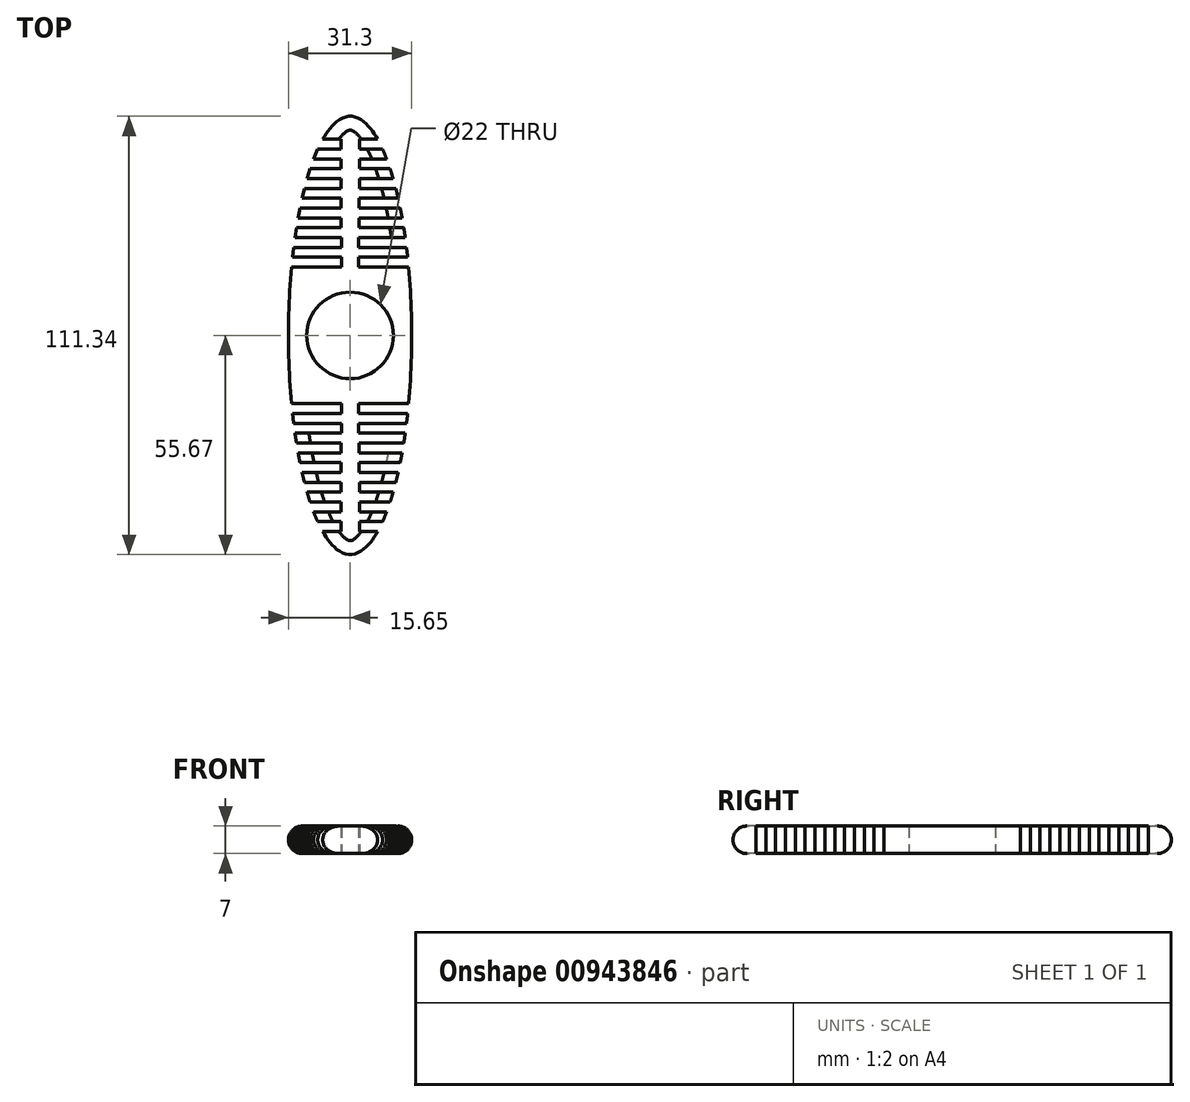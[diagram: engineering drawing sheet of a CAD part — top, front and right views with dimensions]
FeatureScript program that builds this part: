
annotation { "Feature Type Name" : "Feature", "Feature Type Description" : "" }
export const myFeature = defineFeature(function(context is Context, id is Id, definition is map)
    precondition{}
    {
        {
            var Q0;
            Q0=qCreatedBy(makeId("Top.planeOp"),FACE);
            var sketch = newSketch(context, id + "F0", { "sketchPlane" : qUnion([Q0])});
            skCircle(sketch, "E0", {"center": v(0, 0) * mm, "radius": 11 * mm});
            skEllipse(sketch, "E1", {"center": v(0, 0) * mm, "majorRadius": 55.67 * mm, "minorRadius": 15.65 * mm, "majorAxis": v(0, -1)});
            skLineSegment(sketch, "E2", {"start": v(0, 0) * mm, "end": v(0, -55.67) * mm});
            skLineSegment(sketch, "E3", {"start": v(0, -55.67) * mm, "end": v(0, 55.67) * mm});
            skLineSegment(sketch, "E4", {"start": v(-15.65, 0) * mm, "end": v(15.65, 0) * mm});
            skLineSegment(sketch, "E5", {"start": v(-6.98, 49.84) * mm, "end": v(-2.36, 49.84) * mm});
            skLineSegment(sketch, "E6", {"start": v(-2.36, 49.84) * mm, "end": v(-2.36, 47.34) * mm});
            skLineSegment(sketch, "E7", {"start": v(-2.36, 47.34) * mm, "end": v(-8.24, 47.34) * mm});
            skLineSegment(sketch, "E8", {"start": v(-8.24, 47.34) * mm, "end": v(-9.28, 44.84) * mm});
            skLineSegment(sketch, "E9", {"start": v(-9.28, 44.84) * mm, "end": v(-2.36, 44.84) * mm});
            skLineSegment(sketch, "E10", {"start": v(-2.36, 44.84) * mm, "end": v(-2.36, 42.34) * mm});
            skLineSegment(sketch, "E11", {"start": v(-2.36, 42.34) * mm, "end": v(-10.16, 42.34) * mm});
            skLineSegment(sketch, "E12", {"start": v(-10.16, 42.34) * mm, "end": v(-10.93, 39.84) * mm});
            skLineSegment(sketch, "E13", {"start": v(-10.93, 39.84) * mm, "end": v(-2.36, 39.84) * mm});
            skLineSegment(sketch, "E14", {"start": v(-2.36, 39.84) * mm, "end": v(-2.36, 37.34) * mm});
            skLineSegment(sketch, "E15", {"start": v(-2.36, 37.34) * mm, "end": v(-11.6, 37.34) * mm});
            skLineSegment(sketch, "E16", {"start": v(-11.6, 37.34) * mm, "end": v(-12.2, 34.84) * mm});
            skLineSegment(sketch, "E17", {"start": v(-12.2, 34.84) * mm, "end": v(-2.3, 34.84) * mm});
            skLineSegment(sketch, "E18", {"start": v(-2.3, 34.84) * mm, "end": v(-2.3, 32.34) * mm});
            skLineSegment(sketch, "E19", {"start": v(-2.3, 32.34) * mm, "end": v(-12.74, 32.34) * mm});
            skLineSegment(sketch, "E20", {"start": v(-12.74, 32.34) * mm, "end": v(-13.21, 29.84) * mm});
            skLineSegment(sketch, "E21", {"start": v(-13.21, 29.84) * mm, "end": v(-2.3, 29.84) * mm});
            skLineSegment(sketch, "E22", {"start": v(-2.3, 29.84) * mm, "end": v(-2.3, 27.34) * mm});
            skLineSegment(sketch, "E23", {"start": v(-2.3, 27.34) * mm, "end": v(-13.63, 27.34) * mm});
            skLineSegment(sketch, "E24", {"start": v(-13.63, 27.34) * mm, "end": v(-14, 24.84) * mm});
            skLineSegment(sketch, "E25", {"start": v(-14, 24.84) * mm, "end": v(-2.2, 24.84) * mm});
            skLineSegment(sketch, "E26", {"start": v(-2.2, 24.84) * mm, "end": v(-2.2, 22.34) * mm});
            skLineSegment(sketch, "E27", {"start": v(-14.34, 22.34) * mm, "end": v(-2.2, 22.34) * mm});
            skLineSegment(sketch, "E28", {"start": v(-14.62, 19.84) * mm, "end": v(-2.2, 19.84) * mm});
            skLineSegment(sketch, "E29", {"start": v(-2.2, 19.84) * mm, "end": v(-2.2, 17.34) * mm});
            skLineSegment(sketch, "E30", {"start": v(-2.2, 17.34) * mm, "end": v(-14.87, 17.34) * mm});
            skLineSegment(sketch, "E31.MirrorCS", {"start": v(2.36, 49.84) * mm, "end": v(2.36, 47.34) * mm});
            skLineSegment(sketch, "E32.MirrorCS", {"start": v(6.98, 49.84) * mm, "end": v(2.36, 49.84) * mm});
            skLineSegment(sketch, "E33.MirrorCS", {"start": v(2.36, 47.34) * mm, "end": v(8.24, 47.34) * mm});
            skLineSegment(sketch, "E34.MirrorCS", {"start": v(9.28, 44.84) * mm, "end": v(2.36, 44.84) * mm});
            skLineSegment(sketch, "E35.MirrorCS", {"start": v(2.36, 42.34) * mm, "end": v(10.16, 42.34) * mm});
            skLineSegment(sketch, "E36.MirrorCS", {"start": v(2.36, 44.84) * mm, "end": v(2.36, 42.34) * mm});
            skLineSegment(sketch, "E37.MirrorCS", {"start": v(2.36, 39.84) * mm, "end": v(2.36, 37.34) * mm});
            skLineSegment(sketch, "E38.MirrorCS", {"start": v(2.36, 37.34) * mm, "end": v(11.6, 37.34) * mm});
            skLineSegment(sketch, "E39.MirrorCS", {"start": v(10.93, 39.84) * mm, "end": v(2.36, 39.84) * mm});
            skLineSegment(sketch, "E40.MirrorCS", {"start": v(2.3, 34.84) * mm, "end": v(2.3, 32.34) * mm});
            skLineSegment(sketch, "E41.MirrorCS", {"start": v(12.2, 34.84) * mm, "end": v(2.3, 34.84) * mm});
            skLineSegment(sketch, "E42.MirrorCS", {"start": v(2.3, 32.34) * mm, "end": v(12.74, 32.34) * mm});
            skLineSegment(sketch, "E43.MirrorCS", {"start": v(13.21, 29.84) * mm, "end": v(2.3, 29.84) * mm});
            skLineSegment(sketch, "E44.MirrorCS", {"start": v(2.3, 29.84) * mm, "end": v(2.3, 27.34) * mm});
            skLineSegment(sketch, "E45.MirrorCS", {"start": v(2.2, 24.84) * mm, "end": v(2.2, 22.34) * mm});
            skLineSegment(sketch, "E46.MirrorCS", {"start": v(2.3, 27.34) * mm, "end": v(13.63, 27.34) * mm});
            skLineSegment(sketch, "E47.MirrorCS", {"start": v(14.34, 22.34) * mm, "end": v(2.2, 22.34) * mm});
            skLineSegment(sketch, "E48.MirrorCS", {"start": v(14, 24.84) * mm, "end": v(2.2, 24.84) * mm});
            skLineSegment(sketch, "E49.MirrorCS", {"start": v(14.62, 19.84) * mm, "end": v(2.2, 19.84) * mm});
            skLineSegment(sketch, "E50.MirrorCS", {"start": v(2.2, 19.84) * mm, "end": v(2.2, 17.34) * mm});
            skLineSegment(sketch, "E51.MirrorCS", {"start": v(2.2, 17.34) * mm, "end": v(14.87, 17.34) * mm});
            skLineSegment(sketch, "E52.MirrorCS", {"start": v(2.2, -17.34) * mm, "end": v(14.87, -17.34) * mm});
            skLineSegment(sketch, "E53.MirrorCS", {"start": v(-2.2, -17.34) * mm, "end": v(-14.87, -17.34) * mm});
            skLineSegment(sketch, "E54.MirrorCS", {"start": v(2.2, -19.84) * mm, "end": v(2.2, -17.34) * mm});
            skLineSegment(sketch, "E55.MirrorCS", {"start": v(-2.2, -19.84) * mm, "end": v(-2.2, -17.34) * mm});
            skLineSegment(sketch, "E56.MirrorCS", {"start": v(-14.62, -19.84) * mm, "end": v(-2.2, -19.84) * mm});
            skLineSegment(sketch, "E57.MirrorCS", {"start": v(14.62, -19.84) * mm, "end": v(2.2, -19.84) * mm});
            skLineSegment(sketch, "E58.MirrorCS", {"start": v(14.34, -22.34) * mm, "end": v(2.2, -22.34) * mm});
            skLineSegment(sketch, "E59.MirrorCS", {"start": v(14, -24.84) * mm, "end": v(2.2, -24.84) * mm});
            skLineSegment(sketch, "E60.MirrorCS", {"start": v(2.2, -24.84) * mm, "end": v(2.2, -22.34) * mm});
            skLineSegment(sketch, "E61.MirrorCS", {"start": v(-14.34, -22.34) * mm, "end": v(-2.2, -22.34) * mm});
            skLineSegment(sketch, "E62.MirrorCS", {"start": v(-2.2, -24.84) * mm, "end": v(-2.2, -22.34) * mm});
            skLineSegment(sketch, "E63.MirrorCS", {"start": v(-14, -24.84) * mm, "end": v(-2.2, -24.84) * mm});
            skLineSegment(sketch, "E64.MirrorCS", {"start": v(2.3, -27.34) * mm, "end": v(13.63, -27.34) * mm});
            skLineSegment(sketch, "E65.MirrorCS", {"start": v(13.21, -29.84) * mm, "end": v(2.3, -29.84) * mm});
            skLineSegment(sketch, "E66.MirrorCS", {"start": v(2.3, -29.84) * mm, "end": v(2.3, -27.34) * mm});
            skLineSegment(sketch, "E67.MirrorCS", {"start": v(-2.3, -29.84) * mm, "end": v(-2.3, -27.34) * mm});
            skLineSegment(sketch, "E68.MirrorCS", {"start": v(-2.3, -27.34) * mm, "end": v(-13.63, -27.34) * mm});
            skLineSegment(sketch, "E69.MirrorCS", {"start": v(-13.21, -29.84) * mm, "end": v(-2.3, -29.84) * mm});
            skLineSegment(sketch, "E70.MirrorCS", {"start": v(-2.3, -32.34) * mm, "end": v(-12.74, -32.34) * mm});
            skLineSegment(sketch, "E71.MirrorCS", {"start": v(-2.3, -34.84) * mm, "end": v(-2.3, -32.34) * mm});
            skLineSegment(sketch, "E72.MirrorCS", {"start": v(-12.2, -34.84) * mm, "end": v(-2.3, -34.84) * mm});
            skLineSegment(sketch, "E73.MirrorCS", {"start": v(12.2, -34.84) * mm, "end": v(2.3, -34.84) * mm});
            skLineSegment(sketch, "E74.MirrorCS", {"start": v(2.3, -34.84) * mm, "end": v(2.3, -32.34) * mm});
            skLineSegment(sketch, "E75.MirrorCS", {"start": v(2.3, -32.34) * mm, "end": v(12.74, -32.34) * mm});
            skLineSegment(sketch, "E76.MirrorCS", {"start": v(2.36, -37.34) * mm, "end": v(11.6, -37.34) * mm});
            skLineSegment(sketch, "E77.MirrorCS", {"start": v(10.93, -39.84) * mm, "end": v(2.36, -39.84) * mm});
            skLineSegment(sketch, "E78.MirrorCS", {"start": v(-2.36, -39.84) * mm, "end": v(-2.36, -37.34) * mm});
            skLineSegment(sketch, "E79.MirrorCS", {"start": v(-2.36, -37.34) * mm, "end": v(-11.6, -37.34) * mm});
            skLineSegment(sketch, "E80.MirrorCS", {"start": v(-10.93, -39.84) * mm, "end": v(-2.36, -39.84) * mm});
            skLineSegment(sketch, "E81.MirrorCS", {"start": v(-2.36, -42.34) * mm, "end": v(-10.16, -42.34) * mm});
            skLineSegment(sketch, "E82.MirrorCS", {"start": v(2.36, -39.84) * mm, "end": v(2.36, -37.34) * mm});
            skLineSegment(sketch, "E83.MirrorCS", {"start": v(-2.36, -44.84) * mm, "end": v(-2.36, -42.34) * mm});
            skLineSegment(sketch, "E84.MirrorCS", {"start": v(2.36, -44.84) * mm, "end": v(2.36, -42.34) * mm});
            skLineSegment(sketch, "E85.MirrorCS", {"start": v(2.36, -42.34) * mm, "end": v(10.16, -42.34) * mm});
            skLineSegment(sketch, "E86.MirrorCS", {"start": v(9.28, -44.84) * mm, "end": v(2.36, -44.84) * mm});
            skLineSegment(sketch, "E87.MirrorCS", {"start": v(2.36, -47.34) * mm, "end": v(8.24, -47.34) * mm});
            skLineSegment(sketch, "E88.MirrorCS", {"start": v(2.36, -49.84) * mm, "end": v(2.36, -47.34) * mm});
            skLineSegment(sketch, "E89.MirrorCS", {"start": v(6.98, -49.84) * mm, "end": v(2.36, -49.84) * mm});
            skLineSegment(sketch, "E90.MirrorCS", {"start": v(-2.36, -47.34) * mm, "end": v(-8.24, -47.34) * mm});
            skLineSegment(sketch, "E91.MirrorCS", {"start": v(-2.36, -49.84) * mm, "end": v(-2.36, -47.34) * mm});
            skLineSegment(sketch, "E92.MirrorCS", {"start": v(-6.98, -49.84) * mm, "end": v(-2.36, -49.84) * mm});
            skLineSegment(sketch, "E93.MirrorCS", {"start": v(-9.28, -44.84) * mm, "end": v(-2.36, -44.84) * mm});
            skSolve(sketch);
        }
        {
            var Q0;
            {var subQ0=sQuery(id+"F0.wireOp",EDGE,"E5");Q0=makeQuery(id+"F0.imprint","IMPRINT",FACE,{"disambiguationData":[TD([[makeQuery(id+"F0.imprint","IMPRINT",EDGE,{"derivedFrom":subQ0}),1.0]])]});}
            var Q1;
            Q1=makeQuery(id+"F0.imprint","IMPRINT",FACE,{"disambiguationData":[TD([[makeQuery(id+"F0.imprint","IMPRINT",EDGE,{"derivedFrom":sQuery(id+"F0.wireOp",EDGE,"E31.MirrorCS")}),-1.0]])]});
            var Q2;
            {var subQ11=sQuery(id+"F0.wireOp",EDGE,"E52.MirrorCS");Q2=makeQuery(id+"F0.imprint","IMPRINT",FACE,{"disambiguationData":[TD([[makeQuery(id+"F0.imprint","IMPRINT",EDGE,{"derivedFrom":subQ11}),1.0]])]});}
            var Q3;
            {var subQ14=sQuery(id+"F0.wireOp",EDGE,"E53.MirrorCS");Q3=makeQuery(id+"F0.imprint","IMPRINT",FACE,{"disambiguationData":[TD([[makeQuery(id+"F0.imprint","IMPRINT",EDGE,{"derivedFrom":subQ14}),-1.0]])]});}
            extrude(context, id + "F1", {"entities" : qUnion([Q0, Q1, Q2, Q3]), "depth" : 7 * mm, "offsetDistance" : 25 * mm});
        }
        {
            var Q0;
            {var subQ0=sQuery(id+"F0.wireOp",EDGE,"E1");Q0=makeQuery(id+"F1.opExtrude","CAP_EDGE",EDGE,{"disambiguationData":[OSD([subQ0]),TDD([makeQuery(id+"F0.imprint","IMPRINT",EDGE,{"disambiguationData":[TD([[makeQuery(id+"F0.imprint","INTERSECT",VERTEX,{"derivedFrom":[subQ0,sQuery(id+"F0.wireOp",EDGE,"E30")]}),-1.0]])],"derivedFrom":subQ0}),makeQuery(id+"F0.imprint","IMPRINT",EDGE,{"disambiguationData":[TD([[makeQuery(id+"F0.imprint","INTERSECT",VERTEX,{"derivedFrom":[subQ0,sQuery(id+"F0.wireOp",EDGE,"E53.MirrorCS")]}),1.0]])],"derivedFrom":subQ0})])],"isStart":true});}
            var Q1;
            {var subQ0=sQuery(id+"F0.wireOp",EDGE,"E1");Q1=makeQuery(id+"F1.opExtrude","CAP_EDGE",EDGE,{"disambiguationData":[OSD([subQ0]),TDD([makeQuery(id+"F0.imprint","IMPRINT",EDGE,{"disambiguationData":[TD([[makeQuery(id+"F0.imprint","INTERSECT",VERTEX,{"derivedFrom":[subQ0,sQuery(id+"F0.wireOp",EDGE,"E30")]}),-1.0]])],"derivedFrom":subQ0}),makeQuery(id+"F0.imprint","IMPRINT",EDGE,{"disambiguationData":[TD([[makeQuery(id+"F0.imprint","INTERSECT",VERTEX,{"derivedFrom":[subQ0,sQuery(id+"F0.wireOp",EDGE,"E53.MirrorCS")]}),1.0]])],"derivedFrom":subQ0})])],"isStart":false});}
            var Q2;
            {var subQ0=sQuery(id+"F0.wireOp",EDGE,"E1");Q2=makeQuery(id+"F1.opExtrude","CAP_EDGE",EDGE,{"disambiguationData":[OSD([subQ0]),TDD([makeQuery(id+"F0.imprint","IMPRINT",EDGE,{"disambiguationData":[TD([[makeQuery(id+"F0.imprint","INTERSECT",VERTEX,{"derivedFrom":[subQ0,sQuery(id+"F0.wireOp",EDGE,"E90.MirrorCS")]}),1.0]])],"derivedFrom":subQ0})])],"isStart":true});}
            var Q3;
            {var subQ0=sQuery(id+"F0.wireOp",EDGE,"E1");Q3=makeQuery(id+"F1.opExtrude","CAP_EDGE",EDGE,{"disambiguationData":[OSD([subQ0]),TDD([makeQuery(id+"F0.imprint","IMPRINT",EDGE,{"disambiguationData":[TD([[makeQuery(id+"F0.imprint","INTERSECT",VERTEX,{"derivedFrom":[subQ0,sQuery(id+"F0.wireOp",EDGE,"E80.MirrorCS")]}),-1.0]])],"derivedFrom":subQ0})])],"isStart":true});}
            var Q4;
            {var subQ0=sQuery(id+"F0.wireOp",EDGE,"E1");Q4=makeQuery(id+"F1.opExtrude","CAP_EDGE",EDGE,{"disambiguationData":[OSD([subQ0]),TDD([makeQuery(id+"F0.imprint","IMPRINT",EDGE,{"disambiguationData":[TD([[makeQuery(id+"F0.imprint","INTERSECT",VERTEX,{"derivedFrom":[subQ0,sQuery(id+"F0.wireOp",EDGE,"E72.MirrorCS")]}),-1.0]])],"derivedFrom":subQ0})])],"isStart":true});}
            var Q5;
            {var subQ0=sQuery(id+"F0.wireOp",EDGE,"E1");Q5=makeQuery(id+"F1.opExtrude","CAP_EDGE",EDGE,{"disambiguationData":[OSD([subQ0]),TDD([makeQuery(id+"F0.imprint","IMPRINT",EDGE,{"disambiguationData":[TD([[makeQuery(id+"F0.imprint","INTERSECT",VERTEX,{"derivedFrom":[subQ0,sQuery(id+"F0.wireOp",EDGE,"E69.MirrorCS")]}),-1.0]])],"derivedFrom":subQ0})])],"isStart":true});}
            var Q6;
            {var subQ0=sQuery(id+"F0.wireOp",EDGE,"E1");Q6=makeQuery(id+"F1.opExtrude","CAP_EDGE",EDGE,{"disambiguationData":[OSD([subQ0]),TDD([makeQuery(id+"F0.imprint","IMPRINT",EDGE,{"disambiguationData":[TD([[makeQuery(id+"F0.imprint","INTERSECT",VERTEX,{"derivedFrom":[subQ0,sQuery(id+"F0.wireOp",EDGE,"E56.MirrorCS")]}),-1.0]])],"derivedFrom":subQ0})])],"isStart":true});}
            var Q7;
            {var subQ0=sQuery(id+"F0.wireOp",EDGE,"E1");Q7=makeQuery(id+"F1.opExtrude","CAP_EDGE",EDGE,{"disambiguationData":[OSD([subQ0]),TDD([makeQuery(id+"F0.imprint","IMPRINT",EDGE,{"disambiguationData":[TD([[makeQuery(id+"F0.imprint","INTERSECT",VERTEX,{"derivedFrom":[subQ0,sQuery(id+"F0.wireOp",EDGE,"E63.MirrorCS")]}),-1.0]])],"derivedFrom":subQ0})])],"isStart":true});}
            var Q8;
            {var subQ0=sQuery(id+"F0.wireOp",EDGE,"E1");Q8=makeQuery(id+"F1.opExtrude","CAP_EDGE",EDGE,{"disambiguationData":[OSD([subQ0]),TDD([makeQuery(id+"F0.imprint","IMPRINT",EDGE,{"disambiguationData":[TD([[makeQuery(id+"F0.imprint","INTERSECT",VERTEX,{"derivedFrom":[subQ0,sQuery(id+"F0.wireOp",EDGE,"E89.MirrorCS")]}),1.0]])],"derivedFrom":subQ0}),makeQuery(id+"F0.imprint","IMPRINT",EDGE,{"disambiguationData":[TD([[makeQuery(id+"F0.imprint","INTERSECT",VERTEX,{"derivedFrom":[subQ0,sQuery(id+"F0.wireOp",EDGE,"E92.MirrorCS")]}),-1.0]])],"derivedFrom":subQ0})])],"isStart":true});}
            var Q9;
            {var subQ0=sQuery(id+"F0.wireOp",EDGE,"E1");Q9=makeQuery(id+"F1.opExtrude","CAP_EDGE",EDGE,{"disambiguationData":[OSD([subQ0]),TDD([makeQuery(id+"F0.imprint","IMPRINT",EDGE,{"disambiguationData":[TD([[makeQuery(id+"F0.imprint","INTERSECT",VERTEX,{"derivedFrom":[subQ0,sQuery(id+"F0.wireOp",EDGE,"E89.MirrorCS")]}),1.0]])],"derivedFrom":subQ0}),makeQuery(id+"F0.imprint","IMPRINT",EDGE,{"disambiguationData":[TD([[makeQuery(id+"F0.imprint","INTERSECT",VERTEX,{"derivedFrom":[subQ0,sQuery(id+"F0.wireOp",EDGE,"E92.MirrorCS")]}),-1.0]])],"derivedFrom":subQ0})])],"isStart":false});}
            var Q10;
            {var subQ0=sQuery(id+"F0.wireOp",EDGE,"E1");Q10=makeQuery(id+"F1.opExtrude","CAP_EDGE",EDGE,{"disambiguationData":[OSD([subQ0]),TDD([makeQuery(id+"F0.imprint","IMPRINT",EDGE,{"disambiguationData":[TD([[makeQuery(id+"F0.imprint","INTERSECT",VERTEX,{"derivedFrom":[subQ0,sQuery(id+"F0.wireOp",EDGE,"E90.MirrorCS")]}),1.0]])],"derivedFrom":subQ0})])],"isStart":false});}
            var Q11;
            {var subQ0=sQuery(id+"F0.wireOp",EDGE,"E1");Q11=makeQuery(id+"F1.opExtrude","CAP_EDGE",EDGE,{"disambiguationData":[OSD([subQ0]),TDD([makeQuery(id+"F0.imprint","IMPRINT",EDGE,{"disambiguationData":[TD([[makeQuery(id+"F0.imprint","INTERSECT",VERTEX,{"derivedFrom":[subQ0,sQuery(id+"F0.wireOp",EDGE,"E80.MirrorCS")]}),-1.0]])],"derivedFrom":subQ0})])],"isStart":false});}
            var Q12;
            {var subQ0=sQuery(id+"F0.wireOp",EDGE,"E1");Q12=makeQuery(id+"F1.opExtrude","CAP_EDGE",EDGE,{"disambiguationData":[OSD([subQ0]),TDD([makeQuery(id+"F0.imprint","IMPRINT",EDGE,{"disambiguationData":[TD([[makeQuery(id+"F0.imprint","INTERSECT",VERTEX,{"derivedFrom":[subQ0,sQuery(id+"F0.wireOp",EDGE,"E72.MirrorCS")]}),-1.0]])],"derivedFrom":subQ0})])],"isStart":false});}
            var Q13;
            {var subQ0=sQuery(id+"F0.wireOp",EDGE,"E1");Q13=makeQuery(id+"F1.opExtrude","CAP_EDGE",EDGE,{"disambiguationData":[OSD([subQ0]),TDD([makeQuery(id+"F0.imprint","IMPRINT",EDGE,{"disambiguationData":[TD([[makeQuery(id+"F0.imprint","INTERSECT",VERTEX,{"derivedFrom":[subQ0,sQuery(id+"F0.wireOp",EDGE,"E69.MirrorCS")]}),-1.0]])],"derivedFrom":subQ0})])],"isStart":false});}
            var Q14;
            {var subQ0=sQuery(id+"F0.wireOp",EDGE,"E1");Q14=makeQuery(id+"F1.opExtrude","CAP_EDGE",EDGE,{"disambiguationData":[OSD([subQ0]),TDD([makeQuery(id+"F0.imprint","IMPRINT",EDGE,{"disambiguationData":[TD([[makeQuery(id+"F0.imprint","INTERSECT",VERTEX,{"derivedFrom":[subQ0,sQuery(id+"F0.wireOp",EDGE,"E63.MirrorCS")]}),-1.0]])],"derivedFrom":subQ0})])],"isStart":false});}
            var Q15;
            {var subQ0=sQuery(id+"F0.wireOp",EDGE,"E1");Q15=makeQuery(id+"F1.opExtrude","CAP_EDGE",EDGE,{"disambiguationData":[OSD([subQ0]),TDD([makeQuery(id+"F0.imprint","IMPRINT",EDGE,{"disambiguationData":[TD([[makeQuery(id+"F0.imprint","INTERSECT",VERTEX,{"derivedFrom":[subQ0,sQuery(id+"F0.wireOp",EDGE,"E56.MirrorCS")]}),-1.0]])],"derivedFrom":subQ0})])],"isStart":false});}
            var Q16;
            {var subQ0=sQuery(id+"F0.wireOp",EDGE,"E1");Q16=makeQuery(id+"F1.opExtrude","CAP_EDGE",EDGE,{"disambiguationData":[OSD([subQ0]),TDD([makeQuery(id+"F0.imprint","IMPRINT",EDGE,{"disambiguationData":[TD([[makeQuery(id+"F0.imprint","INTERSECT",VERTEX,{"derivedFrom":[subQ0,sQuery(id+"F0.wireOp",EDGE,"E86.MirrorCS")]}),1.0]])],"derivedFrom":subQ0})])],"isStart":false});}
            var Q17;
            {var subQ0=sQuery(id+"F0.wireOp",EDGE,"E1");Q17=makeQuery(id+"F1.opExtrude","CAP_EDGE",EDGE,{"disambiguationData":[OSD([subQ0]),TDD([makeQuery(id+"F0.imprint","IMPRINT",EDGE,{"disambiguationData":[TD([[makeQuery(id+"F0.imprint","INTERSECT",VERTEX,{"derivedFrom":[subQ0,sQuery(id+"F0.wireOp",EDGE,"E86.MirrorCS")]}),1.0]])],"derivedFrom":subQ0})])],"isStart":true});}
            var Q18;
            {var subQ0=sQuery(id+"F0.wireOp",EDGE,"E1");Q18=makeQuery(id+"F1.opExtrude","CAP_EDGE",EDGE,{"disambiguationData":[OSD([subQ0]),TDD([makeQuery(id+"F0.imprint","IMPRINT",EDGE,{"disambiguationData":[TD([[makeQuery(id+"F0.imprint","INTERSECT",VERTEX,{"derivedFrom":[subQ0,sQuery(id+"F0.wireOp",EDGE,"E77.MirrorCS")]}),1.0]])],"derivedFrom":subQ0})])],"isStart":false});}
            var Q19;
            {var subQ0=sQuery(id+"F0.wireOp",EDGE,"E1");Q19=makeQuery(id+"F1.opExtrude","CAP_EDGE",EDGE,{"disambiguationData":[OSD([subQ0]),TDD([makeQuery(id+"F0.imprint","IMPRINT",EDGE,{"disambiguationData":[TD([[makeQuery(id+"F0.imprint","INTERSECT",VERTEX,{"derivedFrom":[subQ0,sQuery(id+"F0.wireOp",EDGE,"E77.MirrorCS")]}),1.0]])],"derivedFrom":subQ0})])],"isStart":true});}
            var Q20;
            {var subQ0=sQuery(id+"F0.wireOp",EDGE,"E1");Q20=makeQuery(id+"F1.opExtrude","CAP_EDGE",EDGE,{"disambiguationData":[OSD([subQ0]),TDD([makeQuery(id+"F0.imprint","IMPRINT",EDGE,{"disambiguationData":[TD([[makeQuery(id+"F0.imprint","INTERSECT",VERTEX,{"derivedFrom":[subQ0,sQuery(id+"F0.wireOp",EDGE,"E73.MirrorCS")]}),1.0]])],"derivedFrom":subQ0})])],"isStart":true});}
            var Q21;
            {var subQ0=sQuery(id+"F0.wireOp",EDGE,"E1");Q21=makeQuery(id+"F1.opExtrude","CAP_EDGE",EDGE,{"disambiguationData":[OSD([subQ0]),TDD([makeQuery(id+"F0.imprint","IMPRINT",EDGE,{"disambiguationData":[TD([[makeQuery(id+"F0.imprint","INTERSECT",VERTEX,{"derivedFrom":[subQ0,sQuery(id+"F0.wireOp",EDGE,"E73.MirrorCS")]}),1.0]])],"derivedFrom":subQ0})])],"isStart":false});}
            var Q22;
            {var subQ0=sQuery(id+"F0.wireOp",EDGE,"E1");Q22=makeQuery(id+"F1.opExtrude","CAP_EDGE",EDGE,{"disambiguationData":[OSD([subQ0]),TDD([makeQuery(id+"F0.imprint","IMPRINT",EDGE,{"disambiguationData":[TD([[makeQuery(id+"F0.imprint","INTERSECT",VERTEX,{"derivedFrom":[subQ0,sQuery(id+"F0.wireOp",EDGE,"E65.MirrorCS")]}),1.0]])],"derivedFrom":subQ0})])],"isStart":false});}
            var Q23;
            {var subQ0=sQuery(id+"F0.wireOp",EDGE,"E1");Q23=makeQuery(id+"F1.opExtrude","CAP_EDGE",EDGE,{"disambiguationData":[OSD([subQ0]),TDD([makeQuery(id+"F0.imprint","IMPRINT",EDGE,{"disambiguationData":[TD([[makeQuery(id+"F0.imprint","INTERSECT",VERTEX,{"derivedFrom":[subQ0,sQuery(id+"F0.wireOp",EDGE,"E65.MirrorCS")]}),1.0]])],"derivedFrom":subQ0})])],"isStart":true});}
            var Q24;
            {var subQ0=sQuery(id+"F0.wireOp",EDGE,"E1");Q24=makeQuery(id+"F1.opExtrude","CAP_EDGE",EDGE,{"disambiguationData":[OSD([subQ0]),TDD([makeQuery(id+"F0.imprint","IMPRINT",EDGE,{"disambiguationData":[TD([[makeQuery(id+"F0.imprint","INTERSECT",VERTEX,{"derivedFrom":[subQ0,sQuery(id+"F0.wireOp",EDGE,"E59.MirrorCS")]}),1.0]])],"derivedFrom":subQ0})])],"isStart":true});}
            var Q25;
            {var subQ0=sQuery(id+"F0.wireOp",EDGE,"E1");Q25=makeQuery(id+"F1.opExtrude","CAP_EDGE",EDGE,{"disambiguationData":[OSD([subQ0]),TDD([makeQuery(id+"F0.imprint","IMPRINT",EDGE,{"disambiguationData":[TD([[makeQuery(id+"F0.imprint","INTERSECT",VERTEX,{"derivedFrom":[subQ0,sQuery(id+"F0.wireOp",EDGE,"E59.MirrorCS")]}),1.0]])],"derivedFrom":subQ0})])],"isStart":false});}
            var Q26;
            {var subQ0=sQuery(id+"F0.wireOp",EDGE,"E1");Q26=makeQuery(id+"F1.opExtrude","CAP_EDGE",EDGE,{"disambiguationData":[OSD([subQ0]),TDD([makeQuery(id+"F0.imprint","IMPRINT",EDGE,{"disambiguationData":[TD([[makeQuery(id+"F0.imprint","INTERSECT",VERTEX,{"derivedFrom":[subQ0,sQuery(id+"F0.wireOp",EDGE,"E57.MirrorCS")]}),1.0]])],"derivedFrom":subQ0})])],"isStart":false});}
            var Q27;
            {var subQ0=sQuery(id+"F0.wireOp",EDGE,"E1");Q27=makeQuery(id+"F1.opExtrude","CAP_EDGE",EDGE,{"disambiguationData":[OSD([subQ0]),TDD([makeQuery(id+"F0.imprint","IMPRINT",EDGE,{"disambiguationData":[TD([[makeQuery(id+"F0.imprint","INTERSECT",VERTEX,{"derivedFrom":[subQ0,sQuery(id+"F0.wireOp",EDGE,"E57.MirrorCS")]}),1.0]])],"derivedFrom":subQ0})])],"isStart":true});}
            var Q28;
            {var subQ0=sQuery(id+"F0.wireOp",EDGE,"E1");var subQ1=makeQuery(id+"F0.imprint","INTERSECT",VERTEX,{"disambiguationData":[OD(0.0)],"derivedFrom":[subQ0,sQuery(id+"F0.wireOp",EDGE,"E4")]});Q28=makeQuery(id+"F1.opExtrude","CAP_EDGE",EDGE,{"disambiguationData":[OSD([subQ0]),TDD([makeQuery(id+"F0.imprint","IMPRINT",EDGE,{"disambiguationData":[TD([[subQ1,1.0]])],"derivedFrom":subQ0}),makeQuery(id+"F0.imprint","IMPRINT",EDGE,{"disambiguationData":[TD([[subQ1,-1.0]])],"derivedFrom":subQ0})])],"isStart":false});}
            var Q29;
            {var subQ0=sQuery(id+"F0.wireOp",EDGE,"E1");var subQ1=makeQuery(id+"F0.imprint","INTERSECT",VERTEX,{"disambiguationData":[OD(0.0)],"derivedFrom":[subQ0,sQuery(id+"F0.wireOp",EDGE,"E4")]});Q29=makeQuery(id+"F1.opExtrude","CAP_EDGE",EDGE,{"disambiguationData":[OSD([subQ0]),TDD([makeQuery(id+"F0.imprint","IMPRINT",EDGE,{"disambiguationData":[TD([[subQ1,1.0]])],"derivedFrom":subQ0}),makeQuery(id+"F0.imprint","IMPRINT",EDGE,{"disambiguationData":[TD([[subQ1,-1.0]])],"derivedFrom":subQ0})])],"isStart":true});}
            fillet(context, id + "F2", {"entities" : qUnion([Q0, Q1, Q2, Q3, Q4, Q5, Q6, Q7, Q8, Q9, Q10, Q11, Q12, Q13, Q14, Q15, Q16, Q17, Q18, Q19, Q20, Q21, Q22, Q23, Q24, Q25, Q26, Q27, Q28, Q29]), "radius" : 3.5 * mm, "tangentPropagation" : true, "allowEdgeOverflow" : false});
        }
        {
            var Q0;
            {var subQ0=sQuery(id+"F0.wireOp",EDGE,"E1");Q0=makeQuery(id+"F1.opExtrude","CAP_EDGE",EDGE,{"disambiguationData":[OSD([subQ0]),TDD([makeQuery(id+"F0.imprint","IMPRINT",EDGE,{"disambiguationData":[TD([[makeQuery(id+"F0.imprint","INTERSECT",VERTEX,{"derivedFrom":[subQ0,sQuery(id+"F0.wireOp",EDGE,"E27")]}),-1.0]])],"derivedFrom":subQ0})])],"isStart":false});}
            var Q1;
            {var subQ0=sQuery(id+"F0.wireOp",EDGE,"E1");Q1=makeQuery(id+"F1.opExtrude","CAP_EDGE",EDGE,{"disambiguationData":[OSD([subQ0]),TDD([makeQuery(id+"F0.imprint","IMPRINT",EDGE,{"disambiguationData":[TD([[makeQuery(id+"F0.imprint","INTERSECT",VERTEX,{"derivedFrom":[subQ0,sQuery(id+"F0.wireOp",EDGE,"E27")]}),-1.0]])],"derivedFrom":subQ0})])],"isStart":true});}
            var Q2;
            Q2=makeQuery(id+"F1.opExtrude","CAP_EDGE",EDGE,{"disambiguationData":[OSD([sQuery(id+"F0.wireOp",EDGE,"E24")])],"isStart":false});
            var Q3;
            Q3=makeQuery(id+"F1.opExtrude","CAP_EDGE",EDGE,{"disambiguationData":[OSD([sQuery(id+"F0.wireOp",EDGE,"E24")])],"isStart":true});
            var Q4;
            Q4=makeQuery(id+"F1.opExtrude","CAP_EDGE",EDGE,{"disambiguationData":[OSD([sQuery(id+"F0.wireOp",EDGE,"E20")])],"isStart":false});
            var Q5;
            Q5=makeQuery(id+"F1.opExtrude","CAP_EDGE",EDGE,{"disambiguationData":[OSD([sQuery(id+"F0.wireOp",EDGE,"E20")])],"isStart":true});
            var Q6;
            Q6=makeQuery(id+"F1.opExtrude","CAP_EDGE",EDGE,{"disambiguationData":[OSD([sQuery(id+"F0.wireOp",EDGE,"E16")])],"isStart":false});
            var Q7;
            Q7=makeQuery(id+"F1.opExtrude","CAP_EDGE",EDGE,{"disambiguationData":[OSD([sQuery(id+"F0.wireOp",EDGE,"E16")])],"isStart":true});
            var Q8;
            Q8=makeQuery(id+"F1.opExtrude","CAP_EDGE",EDGE,{"disambiguationData":[OSD([sQuery(id+"F0.wireOp",EDGE,"E12")])],"isStart":false});
            var Q9;
            Q9=makeQuery(id+"F1.opExtrude","CAP_EDGE",EDGE,{"disambiguationData":[OSD([sQuery(id+"F0.wireOp",EDGE,"E12")])],"isStart":true});
            var Q10;
            Q10=makeQuery(id+"F1.opExtrude","CAP_EDGE",EDGE,{"disambiguationData":[OSD([sQuery(id+"F0.wireOp",EDGE,"E8")])],"isStart":false});
            var Q11;
            Q11=makeQuery(id+"F1.opExtrude","CAP_EDGE",EDGE,{"disambiguationData":[OSD([sQuery(id+"F0.wireOp",EDGE,"E8")])],"isStart":true});
            var Q12;
            {var subQ0=sQuery(id+"F0.wireOp",EDGE,"E1");Q12=makeQuery(id+"F1.opExtrude","CAP_EDGE",EDGE,{"disambiguationData":[OSD([subQ0]),TDD([makeQuery(id+"F0.imprint","IMPRINT",EDGE,{"disambiguationData":[TD([[makeQuery(id+"F0.imprint","INTERSECT",VERTEX,{"derivedFrom":[subQ0,sQuery(id+"F0.wireOp",EDGE,"E32.MirrorCS")]}),-1.0]])],"derivedFrom":subQ0}),makeQuery(id+"F0.imprint","IMPRINT",EDGE,{"disambiguationData":[TD([[makeQuery(id+"F0.imprint","INTERSECT",VERTEX,{"derivedFrom":[subQ0,sQuery(id+"F0.wireOp",EDGE,"E5")]}),1.0]])],"derivedFrom":subQ0})])],"isStart":false});}
            var Q13;
            {var subQ0=sQuery(id+"F0.wireOp",EDGE,"E1");Q13=makeQuery(id+"F1.opExtrude","CAP_EDGE",EDGE,{"disambiguationData":[OSD([subQ0]),TDD([makeQuery(id+"F0.imprint","IMPRINT",EDGE,{"disambiguationData":[TD([[makeQuery(id+"F0.imprint","INTERSECT",VERTEX,{"derivedFrom":[subQ0,sQuery(id+"F0.wireOp",EDGE,"E32.MirrorCS")]}),-1.0]])],"derivedFrom":subQ0}),makeQuery(id+"F0.imprint","IMPRINT",EDGE,{"disambiguationData":[TD([[makeQuery(id+"F0.imprint","INTERSECT",VERTEX,{"derivedFrom":[subQ0,sQuery(id+"F0.wireOp",EDGE,"E5")]}),1.0]])],"derivedFrom":subQ0})])],"isStart":true});}
            var Q14;
            {var subQ0=sQuery(id+"F0.wireOp",EDGE,"E1");Q14=makeQuery(id+"F1.opExtrude","CAP_EDGE",EDGE,{"disambiguationData":[OSD([subQ0]),TDD([makeQuery(id+"F0.imprint","IMPRINT",EDGE,{"disambiguationData":[TD([[makeQuery(id+"F0.imprint","INTERSECT",VERTEX,{"derivedFrom":[subQ0,sQuery(id+"F0.wireOp",EDGE,"E33.MirrorCS")]}),1.0]])],"derivedFrom":subQ0})])],"isStart":false});}
            var Q15;
            {var subQ0=sQuery(id+"F0.wireOp",EDGE,"E1");Q15=makeQuery(id+"F1.opExtrude","CAP_EDGE",EDGE,{"disambiguationData":[OSD([subQ0]),TDD([makeQuery(id+"F0.imprint","IMPRINT",EDGE,{"disambiguationData":[TD([[makeQuery(id+"F0.imprint","INTERSECT",VERTEX,{"derivedFrom":[subQ0,sQuery(id+"F0.wireOp",EDGE,"E33.MirrorCS")]}),1.0]])],"derivedFrom":subQ0})])],"isStart":true});}
            var Q16;
            {var subQ0=sQuery(id+"F0.wireOp",EDGE,"E1");Q16=makeQuery(id+"F1.opExtrude","CAP_EDGE",EDGE,{"disambiguationData":[OSD([subQ0]),TDD([makeQuery(id+"F0.imprint","IMPRINT",EDGE,{"disambiguationData":[TD([[makeQuery(id+"F0.imprint","INTERSECT",VERTEX,{"derivedFrom":[subQ0,sQuery(id+"F0.wireOp",EDGE,"E35.MirrorCS")]}),1.0]])],"derivedFrom":subQ0})])],"isStart":false});}
            var Q17;
            {var subQ0=sQuery(id+"F0.wireOp",EDGE,"E1");Q17=makeQuery(id+"F1.opExtrude","CAP_EDGE",EDGE,{"disambiguationData":[OSD([subQ0]),TDD([makeQuery(id+"F0.imprint","IMPRINT",EDGE,{"disambiguationData":[TD([[makeQuery(id+"F0.imprint","INTERSECT",VERTEX,{"derivedFrom":[subQ0,sQuery(id+"F0.wireOp",EDGE,"E35.MirrorCS")]}),1.0]])],"derivedFrom":subQ0})])],"isStart":true});}
            var Q18;
            {var subQ0=sQuery(id+"F0.wireOp",EDGE,"E1");Q18=makeQuery(id+"F1.opExtrude","CAP_EDGE",EDGE,{"disambiguationData":[OSD([subQ0]),TDD([makeQuery(id+"F0.imprint","IMPRINT",EDGE,{"disambiguationData":[TD([[makeQuery(id+"F0.imprint","INTERSECT",VERTEX,{"derivedFrom":[subQ0,sQuery(id+"F0.wireOp",EDGE,"E38.MirrorCS")]}),1.0]])],"derivedFrom":subQ0})])],"isStart":true});}
            var Q19;
            {var subQ0=sQuery(id+"F0.wireOp",EDGE,"E1");Q19=makeQuery(id+"F1.opExtrude","CAP_EDGE",EDGE,{"disambiguationData":[OSD([subQ0]),TDD([makeQuery(id+"F0.imprint","IMPRINT",EDGE,{"disambiguationData":[TD([[makeQuery(id+"F0.imprint","INTERSECT",VERTEX,{"derivedFrom":[subQ0,sQuery(id+"F0.wireOp",EDGE,"E38.MirrorCS")]}),1.0]])],"derivedFrom":subQ0})])],"isStart":false});}
            var Q20;
            {var subQ0=sQuery(id+"F0.wireOp",EDGE,"E1");Q20=makeQuery(id+"F1.opExtrude","CAP_EDGE",EDGE,{"disambiguationData":[OSD([subQ0]),TDD([makeQuery(id+"F0.imprint","IMPRINT",EDGE,{"disambiguationData":[TD([[makeQuery(id+"F0.imprint","INTERSECT",VERTEX,{"derivedFrom":[subQ0,sQuery(id+"F0.wireOp",EDGE,"E42.MirrorCS")]}),1.0]])],"derivedFrom":subQ0})])],"isStart":false});}
            var Q21;
            {var subQ0=sQuery(id+"F0.wireOp",EDGE,"E1");Q21=makeQuery(id+"F1.opExtrude","CAP_EDGE",EDGE,{"disambiguationData":[OSD([subQ0]),TDD([makeQuery(id+"F0.imprint","IMPRINT",EDGE,{"disambiguationData":[TD([[makeQuery(id+"F0.imprint","INTERSECT",VERTEX,{"derivedFrom":[subQ0,sQuery(id+"F0.wireOp",EDGE,"E46.MirrorCS")]}),1.0]])],"derivedFrom":subQ0})])],"isStart":false});}
            var Q22;
            {var subQ0=sQuery(id+"F0.wireOp",EDGE,"E1");Q22=makeQuery(id+"F1.opExtrude","CAP_EDGE",EDGE,{"disambiguationData":[OSD([subQ0]),TDD([makeQuery(id+"F0.imprint","IMPRINT",EDGE,{"disambiguationData":[TD([[makeQuery(id+"F0.imprint","INTERSECT",VERTEX,{"derivedFrom":[subQ0,sQuery(id+"F0.wireOp",EDGE,"E47.MirrorCS")]}),1.0]])],"derivedFrom":subQ0})])],"isStart":false});}
            var Q23;
            {var subQ0=sQuery(id+"F0.wireOp",EDGE,"E1");Q23=makeQuery(id+"F1.opExtrude","CAP_EDGE",EDGE,{"disambiguationData":[OSD([subQ0]),TDD([makeQuery(id+"F0.imprint","IMPRINT",EDGE,{"disambiguationData":[TD([[makeQuery(id+"F0.imprint","INTERSECT",VERTEX,{"derivedFrom":[subQ0,sQuery(id+"F0.wireOp",EDGE,"E47.MirrorCS")]}),1.0]])],"derivedFrom":subQ0})])],"isStart":true});}
            var Q24;
            {var subQ0=sQuery(id+"F0.wireOp",EDGE,"E1");Q24=makeQuery(id+"F1.opExtrude","CAP_EDGE",EDGE,{"disambiguationData":[OSD([subQ0]),TDD([makeQuery(id+"F0.imprint","IMPRINT",EDGE,{"disambiguationData":[TD([[makeQuery(id+"F0.imprint","INTERSECT",VERTEX,{"derivedFrom":[subQ0,sQuery(id+"F0.wireOp",EDGE,"E46.MirrorCS")]}),1.0]])],"derivedFrom":subQ0})])],"isStart":true});}
            var Q25;
            {var subQ0=sQuery(id+"F0.wireOp",EDGE,"E1");Q25=makeQuery(id+"F1.opExtrude","CAP_EDGE",EDGE,{"disambiguationData":[OSD([subQ0]),TDD([makeQuery(id+"F0.imprint","IMPRINT",EDGE,{"disambiguationData":[TD([[makeQuery(id+"F0.imprint","INTERSECT",VERTEX,{"derivedFrom":[subQ0,sQuery(id+"F0.wireOp",EDGE,"E42.MirrorCS")]}),1.0]])],"derivedFrom":subQ0})])],"isStart":true});}
            fillet(context, id + "F3", {"entities" : qUnion([Q0, Q1, Q2, Q3, Q4, Q5, Q6, Q7, Q8, Q9, Q10, Q11, Q12, Q13, Q14, Q15, Q16, Q17, Q18, Q19, Q20, Q21, Q22, Q23, Q24, Q25]), "radius" : 3.5 * mm, "tangentPropagation" : true, "allowEdgeOverflow" : false});
        }
    });
